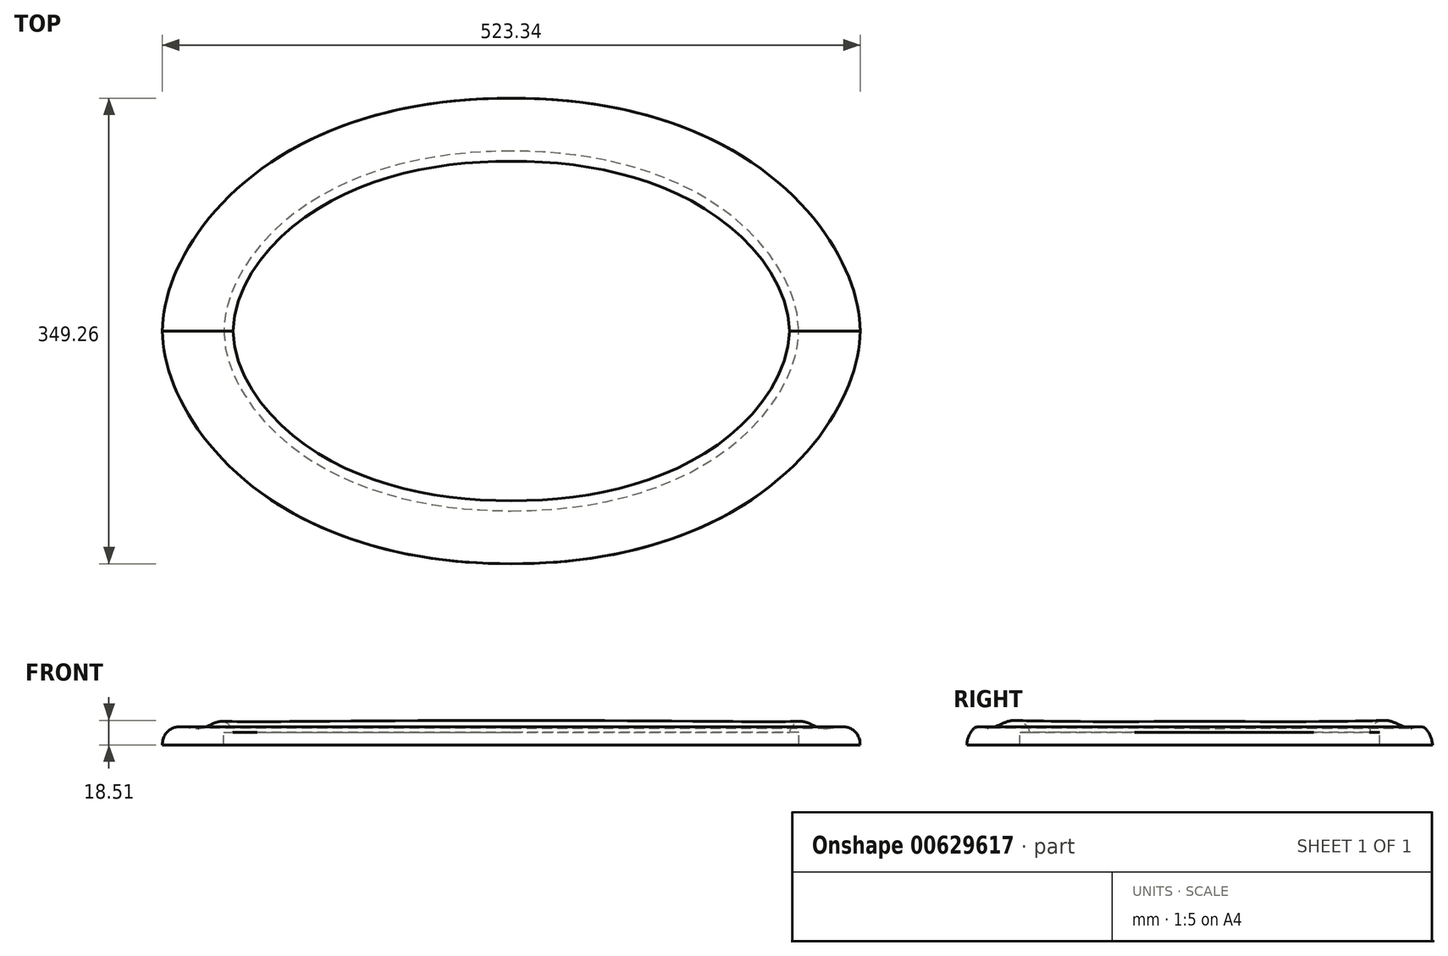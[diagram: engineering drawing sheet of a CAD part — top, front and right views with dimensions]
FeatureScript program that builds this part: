
annotation { "Feature Type Name" : "Feature", "Feature Type Description" : "" }
export const myFeature = defineFeature(function(context is Context, id is Id, definition is map)
    precondition{}
    {
        {
            var Q0;
            Q0=qCreatedBy(makeId("Top.planeOp"),FACE);
            var sketch = newSketch(context, id + "F0", { "sketchPlane" : qUnion([Q0])});
            skEllipticalArc(sketch, "E0", {});
            skEllipticalArc(sketch, "E1", {"construction": true});
            skEllipticalArc(sketch, "E2", {});
            skEllipticalArc(sketch, "E3", {"construction": true});
            const initialGuessF0  = {"E0": [0, 0, 1, 0, 0.206375, 0.127, 3.141592653589793, 4.71238898038469], "E1": [0, 0, 1, 0, 0.206375, 0.127, 4.71238898038469, 0], "E2": [0, 0, 1, 0, 0.206375, 0.127, 0, 1.5707963267948966], "E3": [0, 0, 1, 0, 0.206375, 0.127, 1.5707963267948966, 3.141592653589793]};
            skSetInitialGuess(sketch, initialGuessF0);
            skSolve(sketch);
        }
        {
            var Q0;
            Q0=qCreatedBy(makeId("Front.planeOp"),FACE);
            var sketch = newSketch(context, id + "F1", { "sketchPlane" : qUnion([Q0])});
            skLineSegment(sketch, "E4", {"start": v(-207.7, 0) * mm, "end": v(-261.67, 0) * mm});
            skFitSpline(sketch, "E5", {"points": [v(-261.67, 0) * mm, v(-250.53, 13.67) * mm, v(-233.06, 12.7) * mm, v(-216.9, 17.78) * mm, v(-207.7, 0) * mm], "startDerivative": vector(0.32, 101.91) * mm, "endDerivative": vector(-3.6, -133.31) * mm});
            skSolve(sketch);
        }
        {
            var Q0;
            Q0=qCreatedBy(makeId("Right.planeOp"),FACE);
            var sketch = newSketch(context, id + "F2", { "sketchPlane" : qUnion([Q0])});
            skLineSegment(sketch, "E6", {"start": v(-127, 0) * mm, "end": v(-174.62, 0) * mm});
            skFitSpline(sketch, "E7", {"points": [v(-127, 0) * mm, v(-128.45, 12.7) * mm, v(-140.62, 18.41) * mm, v(-158.1, 12.7) * mm, v(-167.96, 13.33) * mm, v(-174.62, 0) * mm], "startDerivative": vector(-1.26, 52.43) * mm, "endDerivative": vector(0.23, -68.62) * mm});
            skSolve(sketch);
        }
        {
            var Q0;
            Q0=qSketchRegion(id+"F1",true);
            var Q1;
            Q1=qSketchRegion(id+"F2",true);
            var Q2;
            Q2=sQuery(id+"F0.wireOp",EDGE,"E0");
            loft(context, id + "F3", {"startCondition" : LoftEndDerivativeType.NORMAL_TO_PROFILE, "startMagnitude" : 1, "endCondition" : LoftEndDerivativeType.NORMAL_TO_PROFILE, "endMagnitude" : 2.1, "sheetProfilesArray" : [{ "sheetProfileEntities" : qUnion([Q0]) }, { "sheetProfileEntities" : qUnion([Q1]) }], "guidesArray" : [{ "guideEntities" : qUnion([Q2]), "guideDerivativeType" : LoftGuideDerivativeType.DEFAULT, "guideDerivativeMagnitude" : 1 }]});
        }
        {
            var Q0;
            Q0=makeQuery(id+"F3.opLoft","SWEPT_BODY",BODY,{"disambiguationData":[OSD([makeQuery(id+"F1.imprint","IMPRINT",FACE,{"disambiguationData":[TD([[makeQuery(id+"F1.imprint","IMPRINT",EDGE,{"derivedFrom":sQuery(id+"F1.wireOp",EDGE,"E4")}),-1.0]])]}),makeQuery(id+"F2.imprint","IMPRINT",FACE,{"disambiguationData":[TD([[makeQuery(id+"F2.imprint","IMPRINT",EDGE,{"derivedFrom":sQuery(id+"F2.wireOp",EDGE,"E6")}),-1.0]])]})])]});
            var Q1;
            Q1=qCreatedBy(makeId("Front.planeOp"),FACE);
            mirror(context, id + "F4", {"operationType" : NewBodyOperationType.ADD, "entities" : qUnion([Q0]), "mirrorPlane" : qUnion([Q1])});
        }
        {
            var Q0;
            Q0=makeQuery(id+"F3.opLoft","SWEPT_BODY",BODY,{"disambiguationData":[OSD([makeQuery(id+"F1.imprint","IMPRINT",FACE,{"disambiguationData":[TD([[makeQuery(id+"F1.imprint","IMPRINT",EDGE,{"derivedFrom":sQuery(id+"F1.wireOp",EDGE,"E4")}),-1.0]])]}),makeQuery(id+"F2.imprint","IMPRINT",FACE,{"disambiguationData":[TD([[makeQuery(id+"F2.imprint","IMPRINT",EDGE,{"derivedFrom":sQuery(id+"F2.wireOp",EDGE,"E6")}),-1.0]])]})])]});
            var Q1;
            Q1=qCreatedBy(makeId("Right.planeOp"),FACE);
            mirror(context, id + "F5", {"operationType" : NewBodyOperationType.ADD, "entities" : qUnion([Q0]), "mirrorPlane" : qUnion([Q1])});
        }
        {
            var Q0;
            Q0=qCreatedBy(makeId("Right.planeOp"),FACE);
            var sketch = newSketch(context, id + "F6", { "sketchPlane" : qUnion([Q0])});
            skLineSegment(sketch, "E8.bottom", {"start": v(-134.92, 0) * mm, "end": v(-124.76, 0) * mm});
            skLineSegment(sketch, "E8.top", {"start": v(-134.92, 9.53) * mm, "end": v(-124.76, 9.53) * mm});
            skLineSegment(sketch, "E8.left", {"start": v(-134.92, 0) * mm, "end": v(-134.92, 9.53) * mm});
            skLineSegment(sketch, "E8.right", {"start": v(-124.76, 0) * mm, "end": v(-124.76, 9.53) * mm});
            skSolve(sketch);
        }
        {
            var Q0;
            Q0=qSketchRegion(id+"F6",true);
            var Q1;
            {var subQ0=sQuery(id+"F2.wireOp",EDGE,"E7");var subQ1=sQuery(id+"F2.wireOp",EDGE,"E6");var subQ2=sQuery(id+"F1.wireOp",EDGE,"E5");var subQ3=sQuery(id+"F1.wireOp",EDGE,"E4");Q1=makeQuery(id+"F5.opPattern","COPY",EDGE,{"derivedFrom":makeQuery(id+"F3.opLoft","SWEPT_EDGE",EDGE,{"disambiguationData":[OSD([subQ3,subQ2,subQ1,subQ0]),TDD([makeQuery(id+"F1.imprint","INTERSECT",VERTEX,{"disambiguationData":[OD(0.0)],"derivedFrom":[subQ3,subQ2]}),makeQuery(id+"F2.imprint","INTERSECT",VERTEX,{"disambiguationData":[OD(0.0)],"derivedFrom":[subQ1,subQ0]})])]}),"instanceName":"1"});}
            var Q2;
            {var subQ0=sQuery(id+"F2.wireOp",EDGE,"E7");var subQ1=sQuery(id+"F2.wireOp",EDGE,"E6");var subQ2=sQuery(id+"F1.wireOp",EDGE,"E5");var subQ3=sQuery(id+"F1.wireOp",EDGE,"E4");Q2=makeQuery(id+"F3.opLoft","SWEPT_EDGE",EDGE,{"disambiguationData":[OSD([subQ3,subQ2,subQ1,subQ0]),TDD([makeQuery(id+"F1.imprint","INTERSECT",VERTEX,{"disambiguationData":[OD(0.0)],"derivedFrom":[subQ3,subQ2]}),makeQuery(id+"F2.imprint","INTERSECT",VERTEX,{"disambiguationData":[OD(0.0)],"derivedFrom":[subQ1,subQ0]})])]});}
            var Q3;
            {var subQ0=sQuery(id+"F2.wireOp",EDGE,"E7");var subQ1=sQuery(id+"F2.wireOp",EDGE,"E6");var subQ2=sQuery(id+"F1.wireOp",EDGE,"E5");var subQ3=sQuery(id+"F1.wireOp",EDGE,"E4");Q3=makeQuery(id+"F4.opPattern","COPY",EDGE,{"derivedFrom":makeQuery(id+"F3.opLoft","SWEPT_EDGE",EDGE,{"disambiguationData":[OSD([subQ3,subQ2,subQ1,subQ0]),TDD([makeQuery(id+"F1.imprint","INTERSECT",VERTEX,{"disambiguationData":[OD(0.0)],"derivedFrom":[subQ3,subQ2]}),makeQuery(id+"F2.imprint","INTERSECT",VERTEX,{"disambiguationData":[OD(0.0)],"derivedFrom":[subQ1,subQ0]})])]}),"instanceName":"1"});}
            var Q4;
            {var subQ0=sQuery(id+"F2.wireOp",EDGE,"E7");var subQ1=sQuery(id+"F2.wireOp",EDGE,"E6");var subQ2=sQuery(id+"F1.wireOp",EDGE,"E5");var subQ3=sQuery(id+"F1.wireOp",EDGE,"E4");Q4=makeQuery(id+"F5.opPattern","COPY",EDGE,{"derivedFrom":makeQuery(id+"F4.opPattern","COPY",EDGE,{"derivedFrom":makeQuery(id+"F3.opLoft","SWEPT_EDGE",EDGE,{"disambiguationData":[OSD([subQ3,subQ2,subQ1,subQ0]),TDD([makeQuery(id+"F1.imprint","INTERSECT",VERTEX,{"disambiguationData":[OD(0.0)],"derivedFrom":[subQ3,subQ2]}),makeQuery(id+"F2.imprint","INTERSECT",VERTEX,{"disambiguationData":[OD(0.0)],"derivedFrom":[subQ1,subQ0]})])]}),"instanceName":"1"}),"instanceName":"1"});}
            sweep(context, id + "F7", {"operationType" : NewBodyOperationType.REMOVE, "profiles" : qUnion([Q0]), "path" : qUnion([Q1, Q2, Q3, Q4])});
        }
    });
